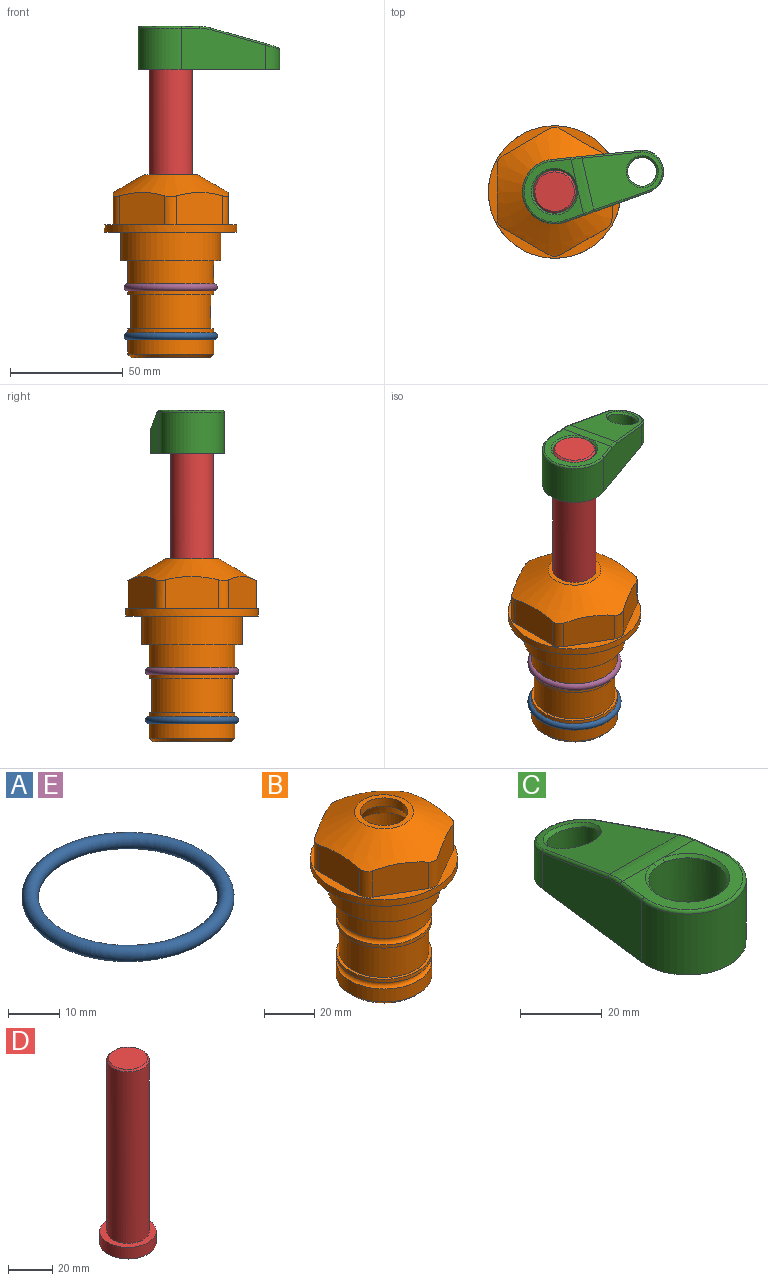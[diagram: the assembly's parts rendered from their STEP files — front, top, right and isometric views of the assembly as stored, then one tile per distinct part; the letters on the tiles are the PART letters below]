
ASSEMBLY  parts=5 mates=4
PART A: 1 faces, bbox 44.7x44.7x3.2 mm
  f0: torus R=19.05mm, axis (0,0,1), area 1193.9mm2
PART B: 36 faces, bbox 58.7x58.7x81 mm
  f0: cylinder r=17.78mm len=35.56mm, axis (0,0,1), area 1670.8mm2, adj f23,f24,f31
  f1: cylinder r=19.05mm len=38.1mm, axis (0,0,1), area 1191.9mm2, adj f26,f27,f30
  f2: plane 58.66x58.66mm, normal (0,0,-1), area 1150.6mm2, adj f3,f28
  f3: cylinder r=29.33mm len=58.66mm, axis (0,0,-1), area 585.1mm2, adj f2,f4
  f4: plane 58.66x58.66mm, normal (0,0,1), area 475.9mm2, adj f3,f5,f6,f7,f8,f9,f10,f11
  f5: plane 20.32x14.34mm, normal (-0.5,0.87,0), area 324.4mm2, adj f4,f15,f16,f17
  f6: plane 20.32x14.34mm, normal (0.5,0.87,0), area 324.4mm2, adj f4,f14,f15,f17
  f7: plane 23.48x14.34mm, normal (1,0,0), area 324.4mm2, adj f4,f13,f14,f17
  f8: plane 20.32x14.34mm, normal (0.5,-0.87,0), area 324.4mm2, adj f4,f12,f13,f17
  f9: plane 20.32x14.34mm, normal (-0.5,-0.87,0), area 324.4mm2, adj f4,f11,f12,f17
  f10: plane 23.48x14.34mm, normal (-1,0,0), area 324.4mm2, adj f4,f11,f16,f17
  f11: cylinder r=5.08mm len=12.85mm, axis (0,0,-1), area 67.2mm2, adj f4,f9,f10,f17
  f12: cylinder r=5.08mm len=12.85mm, axis (0,0,-1), area 67.2mm2, adj f4,f8,f9,f17
  f13: cylinder r=5.08mm len=12.85mm, axis (0,0,-1), area 67.2mm2, adj f4,f7,f8,f17
  f14: cylinder r=5.08mm len=12.85mm, axis (0,0,-1), area 67.2mm2, adj f4,f6,f7,f17
  f15: cylinder r=5.08mm len=12.85mm, axis (0,0,-1), area 67.2mm2, adj f4,f5,f6,f17
  f16: cylinder r=5.08mm len=12.85mm, axis (0,0,-1), area 67.2mm2, adj f4,f5,f10,f17
  f17: cone r=11.73mm half-angle=60deg, axis (0,0,-1), area 2071.8mm2, adj f5,f6,f7,f8,f9,f10,f11,f12
  f18: plane 23.46x23.46mm, normal (0,0,1), area 147.4mm2, adj f17,f35
  f19: plane 34.93x34.93mm, normal (0,0,-1), area 958mm2, adj f29
  f20: cylinder r=19.05mm len=38.1mm, axis (0,0,1), area 760.1mm2, adj f21,f29
  f21: torus R=19.05mm, axis (0,0,1), area 565.3mm2, adj f20,f22
  f22: cylinder r=19.05mm len=38.1mm, axis (0,0,1), area 190mm2, adj f21,f23
  f23: plane 38.1x38.1mm, normal (0,0,1), area 146.9mm2, adj f0,f22
  f24: plane 38.1x38.1mm, normal (0,0,-1), area 146.9mm2, adj f0,f25
  f25: cylinder r=19.05mm len=38.1mm, axis (0,0,1), area 190mm2, adj f24,f26
  f26: torus R=19.05mm, axis (0,0,1), area 565.3mm2, adj f1,f25
  f27: plane 44.45x44.45mm, normal (0,0,-1), area 411.7mm2, adj f1,f28
  f28: cylinder r=22.23mm len=44.45mm, axis (0,0,1), area 1773.5mm2, adj f2,f27
  f29: cone r=19.05mm half-angle=45deg, axis (0,0,1), area 257.5mm2, adj f19,f20
  f30: cylinder r=3.17mm len=6.75mm, axis (-1,0,0), area 128mm2, adj f1,f33
  f31: cylinder r=3.17mm len=6.35mm, axis (-1,0,0), area 102.5mm2, adj f0,f33
  f32: plane 25.4x25.4mm, normal (0,0,1), area 506.7mm2, adj f33
  f33: cylinder r=12.7mm len=66.42mm, axis (0,0,-1), area 5236.2mm2, adj f30,f31,f32,f34
  f34: cone r=9.53mm half-angle=30deg, axis (0,0,-1), area 443.4mm2, adj f33,f35
  f35: cylinder r=9.53mm len=19.05mm, axis (0,0,-1), area 240.9mm2, adj f18,f34
PART C: 31 faces, bbox 31.7x65.5x19.8 mm
  f0: plane 39.12x18.26mm, normal (0.99,0.12,0), area 612.2mm2, adj f1,f4,f7,f11,f13,f15
  f1: cylinder r=9.53mm len=18.91mm, axis (0,0,-1), area 296.1mm2, adj f0,f2,f7,f17
  f2: plane 39.12x18.26mm, normal (-0.99,0.12,0), area 612.2mm2, adj f1,f4,f7,f12,f14,f16
  f3: cylinder r=6.35mm len=12.7mm, axis (0,0,-1), area 362.4mm2, adj f7,f18
  f4: cylinder r=14.29mm len=28.58mm, axis (0,0,-1), area 882.2mm2, adj f0,f2,f7,f10
  f5: cylinder r=9.53mm len=19.05mm, axis (0,0,-1), area 1092.6mm2, adj f7,f19,f20
  f6: plane 26.99x23.69mm, normal (0,0,1), area 216.2mm2, adj f9,f10,f11,f12,f19
  f7: plane 63.5x28.58mm, normal (0,0,-1), area 661.8mm2, adj f0,f1,f2,f3,f4,f5,f22,f23
  f8: plane 33.52x23.6mm, normal (0,0.26,0.97), area 486mm2, adj f9,f15,f16,f17,f18
  f9: cylinder r=19.05mm len=24.72mm, axis (1,0,0), area 120.4mm2, adj f6,f8,f13,f14,f20
  f10: torus R=13.49mm, axis (0,0,1), area 59mm2, adj f4,f6,f11,f12
  f11: cylinder r=0.79mm len=8.67mm, axis (0.12,-0.99,0), area 10.8mm2, adj f0,f6,f10,f13
  f12: cylinder r=0.79mm len=8.67mm, axis (0.12,0.99,0), area 10.8mm2, adj f2,f6,f10,f14
  f13: bspline ~4.95x1.42mm, area 6.1mm2, adj f0,f9,f11,f15
  f14: bspline ~4.95x1.42mm, area 6.1mm2, adj f2,f9,f12,f16
  f15: cylinder r=0.79mm len=25.95mm, axis (0.12,-0.96,0.26), area 32.9mm2, adj f0,f8,f13,f17
  f16: cylinder r=0.79mm len=25.95mm, axis (0.12,0.96,-0.26), area 32.9mm2, adj f2,f8,f14,f17
  f17: bspline ~18.91x8.38mm, area 30mm2, adj f1,f8,f15,f16
  f18: bspline ~14.29x14.29mm, area 48.3mm2, adj f3,f8
  f19: cone r=9.53mm half-angle=45deg, axis (0,0,1), area 66.5mm2, adj f5,f6,f20
  f20: bspline ~3.22x0.96mm, area 3.5mm2, adj f5,f9,f19
  f21: plane 2.75x2.72mm, normal (0,0,-1), area 2.9mm2, adj f23,f25,f28
  f22: plane 23.05x15.88mm, normal (-0.99,-0.12,0), area 323.6mm2, adj f7,f25,f26,f27,f28,f29
  f23: plane 23.05x15.88mm, normal (0.99,-0.12,0), area 323.6mm2, adj f7,f21,f25,f27,f28,f30
  f24: cylinder r=9.53mm len=10.69mm, axis (0,0,-1), area 114.7mm2, adj f7,f27,f29,f30
  f25: cylinder r=12.7mm len=20.59mm, axis (0,0,-1), area 381.1mm2, adj f7,f21,f22,f23,f26,f28
  f26: plane 2.75x2.72mm, normal (0,0,-1), area 2.9mm2, adj f22,f25,f28
  f27: plane 19.72x18.37mm, normal (0,-0.26,-0.97), area 291.8mm2, adj f22,f23,f24,f28,f29,f30
  f28: cylinder r=15.88mm len=19.92mm, axis (1,0,0), area 54.8mm2, adj f21,f22,f23,f25,f26,f27
  f29: cylinder r=1.59mm len=11mm, axis (0,0,-1), area 34.7mm2, adj f7,f22,f24,f27
  f30: cylinder r=1.59mm len=11mm, axis (0,0,-1), area 34.7mm2, adj f7,f23,f24,f27
PART D: 6 faces, bbox 25.4x25.4x101.6 mm
  f0: plane 17.46x17.46mm, normal (0,0,1), area 239.5mm2, adj f5
  f1: plane 25.4x25.4mm, normal (0,0,-1), area 506.7mm2, adj f2
  f2: cylinder r=12.7mm len=25.4mm, axis (0,0,1), area 506.7mm2, adj f1,f3
  f3: plane 25.4x25.4mm, normal (0,0,1), area 221.7mm2, adj f2,f4
  f4: cylinder r=9.53mm len=94.46mm, axis (0,0,1), area 5653mm2, adj f3,f5
  f5: cone r=8.73mm half-angle=45deg, axis (0,0,-1), area 64.4mm2, adj f0,f4
PART E: same geometry as A
PLACE A t=(0,0,-21.59)mm
PLACE B at identity fixed
PLACE C rot(axis=(0,0,-1),77.2deg) t=(0,0,27.55)mm
PLACE D rot(axis=(0,0,-1),77.2deg) t=(0,0,27.55)mm
PLACE E at identity
MATE fastened D.f2 <-> C.f4  axis (0,0,1) through (0,0,91.05)mm
MATE fastened E.f0 <-> B.f0  axis (0,0,1) through (0,0,-24.51)mm
MATE fastened A.f0 <-> B.f0  axis (0,0,1) through (0,0,-46.1)mm
MATE cylindrical D.f2 <-> B.f0  axis (0,0,-1) through (0,0,-10.55)mm
